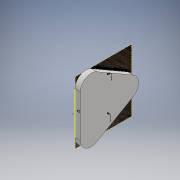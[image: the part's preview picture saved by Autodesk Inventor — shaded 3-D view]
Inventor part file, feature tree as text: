
AUTODESK INVENTOR PART (.ipt)
format: ipt  version: 2018 (Build 220112000, 112)  size: 240,640 bytes
history: native  units: mm
features: sketch x4, extrude x1, fillet x1, other x1
ambient origin geometry x8: Origin, YZ Plane, XZ Plane, XY Plane, X Axis, Y Axis, Z Axis, Center Point
bodies: Solid1 (feature_tree)
feature tree (7):
  extrude  "Extrusion1"  Depth=1.5mm TaperAngle=0.0deg
  fillet  "Fillet1"  Radius=3.0mm
  sketch  "Sketch2"  dims[d126=1.0mm]
  sketch  "Sketch3"  dims[d127=1.0mm]
  sketch  "Sketch4"  dims[d128=1.0mm]
  sketch  "Sketch1"  dims[d0=12.7mm d1=1.5mm d2=0.0mm d3=3.0mm]
  other  "Image2"
